# Revit family: QF_TRUE_T-23DT-G-HC~FGD01
name_source: partatom
category: Specialty Equipment
revit_build: Autodesk Revit 2015 (Build: 20140606_1530(x64)
units: mm (PartAtom-declared; Revit-internal decimal feet)

## types (1)
- T-23DT-G-HC~FGD01_115/60/1'
    Apparent Power = 725 VA
    Conn Conduit = Yes
    Conn Plug = NEMA 5-15P
    Cycle = 60 Hz
    Depth = 31 13/16"
    Description = REACH-IN COMBINATION HALF SWING DOOR REFRIGERATOR WITH HYDROCARBON REFRIGERANT~FRAMED GLASS DOOR VERSION 01
    Elec Conn Connection Height = 0"
    Elec Conn RI Height = 0"
    FL Amps = 6 A
    Foodservice Equipment Identifier = Yes
    HP = 1/2
    Height = 83 11/32"
    Identify Quantity as Lot = Yes
    Length = 27 1/32"
    Manufacturer = TRUE
    Max Overcurrent Protection = 0 A
    Min Ckt Ampacity = 0 A
    Model = T-23DT-G-HC~FGD01
    Number of Poles = 1
    Phase = 1
    Volts = 115 V
    Watts = 725 W
    Weight in Pounds = 380

## geometry (parser evidence)
native form markers: Sweep x27
no freeform markers — native parametric forms only
